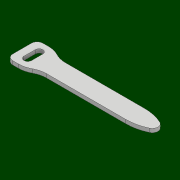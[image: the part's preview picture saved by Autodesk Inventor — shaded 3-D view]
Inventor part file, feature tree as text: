
AUTODESK INVENTOR PART (.ipt)
format: ipt  version: 2018 (Build 220112000, 112)  size: 110,592 bytes
history: native  units: mm
features: other x1, extrude x1, fillet x1, sketch x1
ambient origin geometry x8: Origin, YZ Plane, XZ Plane, XY Plane, X Axis, Y Axis, Z Axis, Center Point
bodies: Body1 (feature_tree)
feature tree (4):
  other  "ソリッド1"
  extrude  "押し出し1"  Depth=4.0mm
  fillet  "フィレット1"  Radius=10.0mm
  sketch  "スケッチ1"
